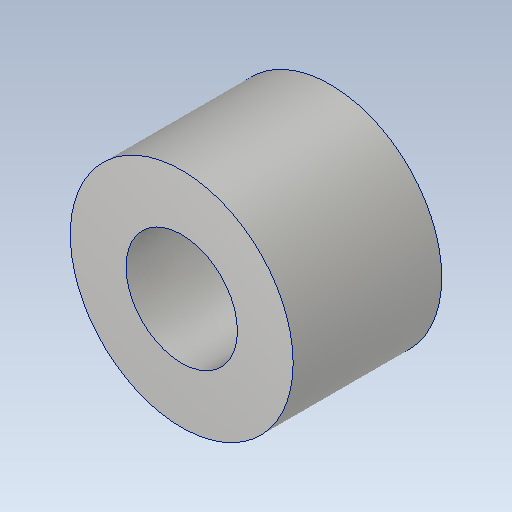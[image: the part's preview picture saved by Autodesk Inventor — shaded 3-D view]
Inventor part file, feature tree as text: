
AUTODESK INVENTOR PART (.ipt)
format: ipt  version: 2020.2 (Build 242310000, 310)  size: 120,832 bytes
history: native  units: mm
features: other x1, extrude x1, sketch x1
ambient origin geometry x8: Origin, YZ Plane, XZ Plane, XY Plane, X Axis, Y Axis, Z Axis, Center Point
bodies: Body1 (feature_tree)
feature tree (3):
  other  "ソリッド1"
  extrude  "押し出し1"  Depth=6.0mm
  sketch  "スケッチ1"
